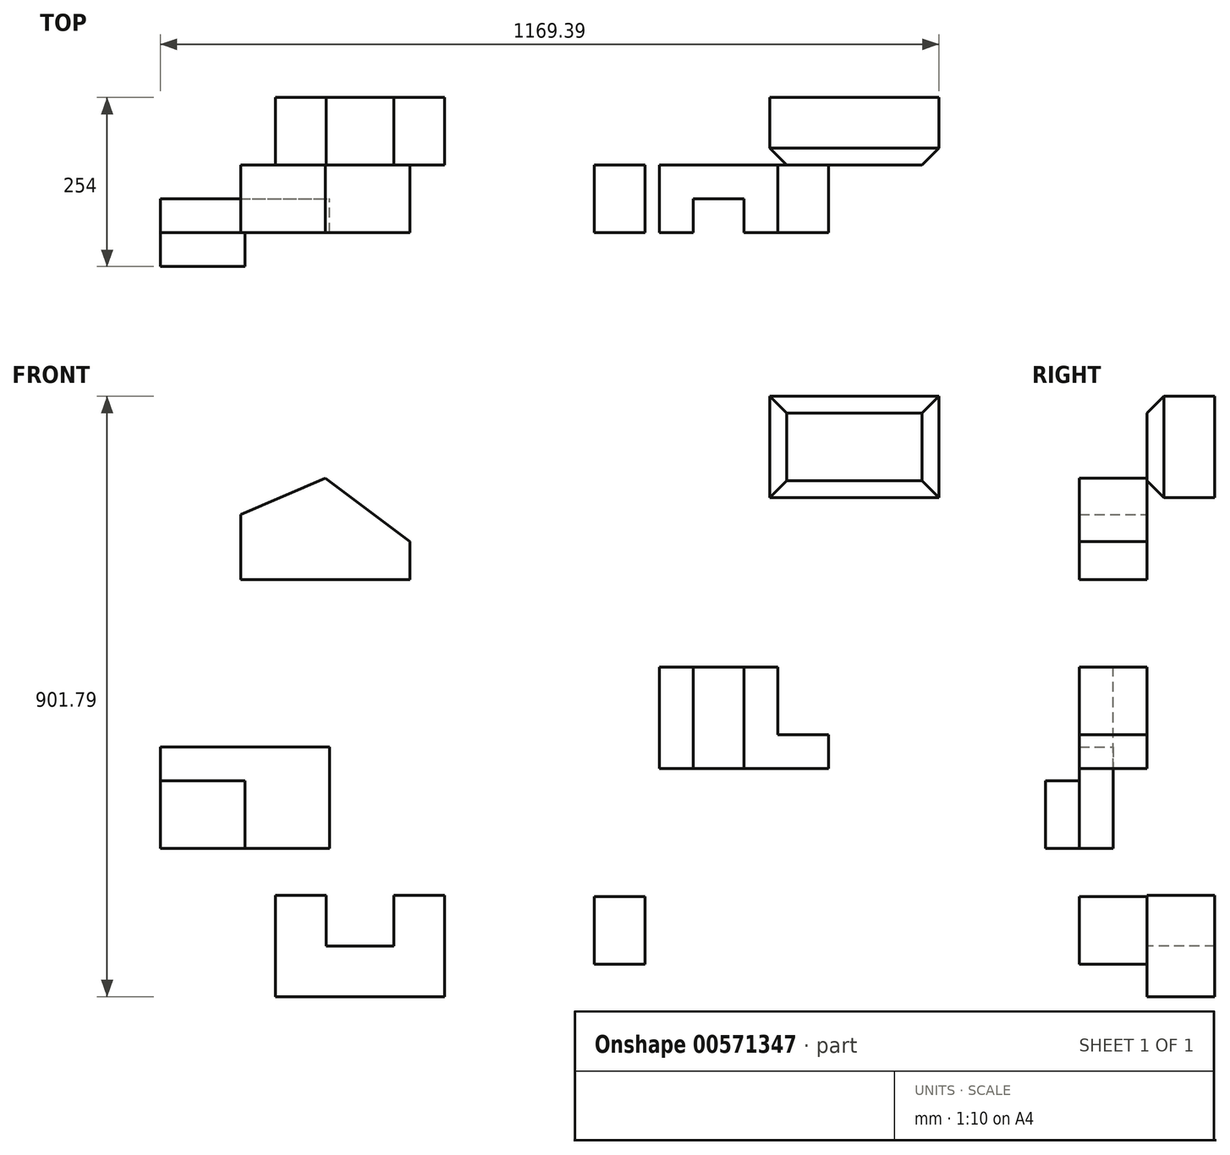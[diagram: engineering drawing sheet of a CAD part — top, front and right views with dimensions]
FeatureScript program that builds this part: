
annotation { "Feature Type Name" : "Feature", "Feature Type Description" : "" }
export const myFeature = defineFeature(function(context is Context, id is Id, definition is map)
    precondition{}
    {
        {
            var Q0;
            Q0=qCreatedBy(makeId("Front.planeOp"),FACE);
            var sketch = newSketch(context, id + "F0", { "sketchPlane" : qUnion([Q0])});
            skLineSegment(sketch, "E0", {"start": v(0, 0) * mm, "end": v(254, 0) * mm});
            skLineSegment(sketch, "E1", {"start": v(254, 152.4) * mm, "end": v(254, 0) * mm});
            skLineSegment(sketch, "E2", {"start": v(254, 152.4) * mm, "end": v(177.8, 152.4) * mm});
            skLineSegment(sketch, "E3", {"start": v(177.8, 152.4) * mm, "end": v(177.8, 76.2) * mm});
            skLineSegment(sketch, "E4", {"start": v(177.8, 76.2) * mm, "end": v(76.2, 76.2) * mm});
            skLineSegment(sketch, "E5", {"start": v(76.2, 76.2) * mm, "end": v(76.2, 152.4) * mm});
            skLineSegment(sketch, "E6", {"start": v(76.2, 132.49) * mm, "end": v(76.2, 125.11) * mm});
            skLineSegment(sketch, "E7", {"start": v(76.2, 152.4) * mm, "end": v(0, 152.4) * mm});
            skLineSegment(sketch, "E8", {"start": v(0, 0) * mm, "end": v(0, 152.4) * mm});
            skSolve(sketch);
        }
        {
            var Q0;
            Q0=makeQuery(id+"F0.imprint","IMPRINT",FACE,{"disambiguationData":[TD([[makeQuery(id+"F0.imprint","IMPRINT",EDGE,{"derivedFrom":sQuery(id+"F0.wireOp",EDGE,"E0")}),1.0]])]});
            extrude(context, id + "F1", {"entities" : qUnion([Q0]), "oppositeDirection" : true, "depth" : 101.6 * mm, "offsetDistance" : 25.4 * mm});
        }
        {
            var Q0;
            Q0=qCreatedBy(makeId("Front.planeOp"),FACE);
            var sketch = newSketch(context, id + "F2", { "sketchPlane" : qUnion([Q0])});
            skLineSegment(sketch, "E9.bottom", {"start": v(-172.87, 375.03) * mm, "end": v(81.13, 375.03) * mm});
            skLineSegment(sketch, "E9.top", {"start": v(-172.87, 222.63) * mm, "end": v(81.13, 222.63) * mm});
            skLineSegment(sketch, "E9.left", {"start": v(-172.87, 375.03) * mm, "end": v(-172.87, 222.63) * mm});
            skLineSegment(sketch, "E9.right", {"start": v(81.13, 375.03) * mm, "end": v(81.13, 222.63) * mm});
            skSolve(sketch);
        }
        {
            var Q0;
            Q0=makeQuery(id+"F2.imprint","IMPRINT",FACE,{"disambiguationData":[TD([[makeQuery(id+"F2.imprint","IMPRINT",EDGE,{"derivedFrom":sQuery(id+"F2.wireOp",EDGE,"E9.bottom")}),-1.0]])]});
            extrude(context, id + "F3", {"entities" : qUnion([Q0]), "depth" : 152.4 * mm, "offsetDistance" : 25.4 * mm});
        }
        {
            var Q0;
            Q0=makeQuery(id+"F3.opExtrude","SWEPT_FACE",FACE,{"disambiguationData":[OSD([sQuery(id+"F2.wireOp",EDGE,"E9.bottom")])]});
            var sketch = newSketch(context, id + "F4", { "sketchPlane" : qUnion([Q0])});
            skLineSegment(sketch, "E10.bottom", {"start": v(81.13, -152.4) * mm, "end": v(-45.87, -152.4) * mm});
            skLineSegment(sketch, "E10.top", {"start": v(81.13, -101.6) * mm, "end": v(-45.87, -101.6) * mm});
            skLineSegment(sketch, "E10.left", {"start": v(81.13, -152.4) * mm, "end": v(81.13, -101.6) * mm});
            skLineSegment(sketch, "E10.right", {"start": v(-45.87, -152.4) * mm, "end": v(-45.87, -101.6) * mm});
            skLineSegment(sketch, "E11.bottom", {"start": v(81.13, 0) * mm, "end": v(-172.87, 0) * mm});
            skLineSegment(sketch, "E11.top", {"start": v(81.13, -39.4) * mm, "end": v(-172.87, -39.4) * mm});
            skLineSegment(sketch, "E11.left", {"start": v(81.13, 0) * mm, "end": v(81.13, -39.4) * mm});
            skLineSegment(sketch, "E11.right", {"start": v(-172.87, 0) * mm, "end": v(-172.87, -39.4) * mm});
            skSolve(sketch);
        }
        {
            var Q0;
            Q0=makeQuery(id+"F4.imprint","IMPRINT",FACE,{"disambiguationData":[TD([[makeQuery(id+"F4.imprint","IMPRINT",EDGE,{"derivedFrom":sQuery(id+"F4.wireOp",EDGE,"E10.bottom")}),1.0]])]});
            extrude(context, id + "F5", {"entities" : qUnion([Q0]), "operationType" : NewBodyOperationType.REMOVE, "oppositeDirection" : true, "depth" : 152.4 * mm, "offsetDistance" : 25.4 * mm});
        }
        {
            var Q0;
            Q0=makeQuery(id+"F3.opExtrude","CAP_FACE",FACE,{"disambiguationData":[OSD([sQuery(id+"F2.wireOp",EDGE,"E9.bottom"),sQuery(id+"F2.wireOp",EDGE,"E9.top"),sQuery(id+"F2.wireOp",EDGE,"E9.left"),sQuery(id+"F2.wireOp",EDGE,"E9.right")])],"isStart":false});
            var sketch = newSketch(context, id + "F6", { "sketchPlane" : qUnion([Q0])});
            skLineSegment(sketch, "E12.bottom", {"start": v(-172.87, 375.03) * mm, "end": v(-45.87, 375.03) * mm});
            skLineSegment(sketch, "E12.top", {"start": v(-172.87, 324.4) * mm, "end": v(-45.87, 324.4) * mm});
            skLineSegment(sketch, "E12.left", {"start": v(-172.87, 375.03) * mm, "end": v(-172.87, 324.4) * mm});
            skLineSegment(sketch, "E12.right", {"start": v(-45.87, 375.03) * mm, "end": v(-45.87, 324.4) * mm});
            skSolve(sketch);
        }
        {
            var Q0;
            Q0 = qSketchRegion(id + "F6", true);
            extrude(context, id + "F7", {"entities" : qUnion([Q0]), "operationType" : NewBodyOperationType.REMOVE, "oppositeDirection" : true, "depth" : 50.8 * mm, "offsetDistance" : 25.4 * mm});
        }
        {
            var Q0;
            Q0 = qSketchRegion(id + "F2", true);
            extrude(context, id + "F8", {"entities" : qUnion([Q0]), "operationType" : NewBodyOperationType.REMOVE, "depth" : 50.8 * mm, "offsetDistance" : 25.4 * mm});
        }
        {
            var Q0;
            Q0=qCreatedBy(makeId("Front.planeOp"),FACE);
            var sketch = newSketch(context, id + "F9", { "sketchPlane" : qUnion([Q0])});
            skLineSegment(sketch, "E13.bottom", {"start": v(576.31, 342.9) * mm, "end": v(830.31, 342.9) * mm});
            skLineSegment(sketch, "E13.top", {"start": v(576.31, 495.3) * mm, "end": v(830.31, 495.3) * mm});
            skLineSegment(sketch, "E13.left", {"start": v(576.31, 342.9) * mm, "end": v(576.31, 495.3) * mm});
            skLineSegment(sketch, "E13.right", {"start": v(830.31, 342.9) * mm, "end": v(830.31, 495.3) * mm});
            skLineSegment(sketch, "E14.right", {"start": v(830.31, 508.38) * mm, "end": v(830.31, 393.7) * mm});
            skLineSegment(sketch, "E15.bottom", {"start": v(754.11, 495.3) * mm, "end": v(830.31, 495.3) * mm});
            skLineSegment(sketch, "E15.top", {"start": v(754.11, 393.7) * mm, "end": v(830.31, 393.7) * mm});
            skLineSegment(sketch, "E15.left", {"start": v(754.11, 495.3) * mm, "end": v(754.11, 393.7) * mm});
            skLineSegment(sketch, "E15.right", {"start": v(830.31, 495.3) * mm, "end": v(830.31, 393.7) * mm});
            skSolve(sketch);
        }
        {
            var Q0;
            Q0=makeQuery(id+"F9.imprint","IMPRINT",FACE,{"disambiguationData":[TD([[makeQuery(id+"F9.imprint","IMPRINT",EDGE,{"derivedFrom":sQuery(id+"F9.wireOp",EDGE,"E13.bottom")}),1.0]])]});
            extrude(context, id + "F10", {"entities" : qUnion([Q0]), "depth" : 101.6 * mm, "offsetDistance" : 25.4 * mm});
        }
        {
            var Q0;
            Q0=makeQuery(id+"F10.opExtrude","SWEPT_FACE",FACE,{"disambiguationData":[OSD([sQuery(id+"F9.wireOp",EDGE,"E13.top")])]});
            var sketch = newSketch(context, id + "F11", { "sketchPlane" : qUnion([Q0])});
            skLineSegment(sketch, "E16.bottom", {"start": v(627.11, -101.6) * mm, "end": v(703.31, -101.6) * mm});
            skLineSegment(sketch, "E16.top", {"start": v(627.11, -50.8) * mm, "end": v(703.31, -50.8) * mm});
            skLineSegment(sketch, "E16.left", {"start": v(627.11, -101.6) * mm, "end": v(627.11, -50.8) * mm});
            skLineSegment(sketch, "E16.right", {"start": v(703.31, -101.6) * mm, "end": v(703.31, -50.8) * mm});
            skSolve(sketch);
        }
        {
            var Q0;
            Q0=makeQuery(id+"F11.imprint","IMPRINT",FACE,{"disambiguationData":[TD([[makeQuery(id+"F11.imprint","IMPRINT",EDGE,{"derivedFrom":sQuery(id+"F11.wireOp",EDGE,"E16.bottom")}),1.0]])]});
            extrude(context, id + "F12", {"entities" : qUnion([Q0]), "operationType" : NewBodyOperationType.REMOVE, "oppositeDirection" : true, "depth" : 152.4 * mm, "offsetDistance" : 25.4 * mm});
        }
        {
            var Q0;
            Q0=qCreatedBy(makeId("Front.planeOp"),FACE);
            var sketch = newSketch(context, id + "F13", { "sketchPlane" : qUnion([Q0])});
            skLineSegment(sketch, "E17.bottom", {"start": v(478.85, 48.86) * mm, "end": v(732.85, 48.86) * mm});
            skLineSegment(sketch, "E17.top", {"start": v(478.85, 201.26) * mm, "end": v(732.85, 201.26) * mm});
            skLineSegment(sketch, "E17.left", {"start": v(478.85, 48.86) * mm, "end": v(478.85, 201.26) * mm});
            skLineSegment(sketch, "E17.right", {"start": v(732.85, 48.86) * mm, "end": v(732.85, 201.26) * mm});
            skLineSegment(sketch, "E18.bottom", {"start": v(478.85, 150.46) * mm, "end": v(555.05, 150.46) * mm});
            skLineSegment(sketch, "E18.top", {"start": v(478.85, 48.86) * mm, "end": v(555.05, 48.86) * mm});
            skLineSegment(sketch, "E18.left", {"start": v(478.85, 150.46) * mm, "end": v(478.85, 48.86) * mm});
            skLineSegment(sketch, "E18.right", {"start": v(555.05, 150.46) * mm, "end": v(555.05, 48.86) * mm});
            skLineSegment(sketch, "E19.bottom", {"start": v(732.85, 201.26) * mm, "end": v(656.65, 201.26) * mm});
            skLineSegment(sketch, "E19.top", {"start": v(732.85, 99.66) * mm, "end": v(656.65, 99.66) * mm});
            skLineSegment(sketch, "E19.left", {"start": v(732.85, 201.26) * mm, "end": v(732.85, 99.66) * mm});
            skLineSegment(sketch, "E19.right", {"start": v(656.65, 201.26) * mm, "end": v(656.65, 99.66) * mm});
            skSolve(sketch);
        }
        {
            var Q0;
            Q0=makeQuery(id+"F13.imprint","IMPRINT",FACE,{"disambiguationData":[TD([[makeQuery(id+"F13.imprint","IMPRINT",EDGE,{"derivedFrom":sQuery(id+"F13.wireOp",EDGE,"E17.bottom")}),1.0]])]});
            extrude(context, id + "F14", {"entities" : qUnion([Q0]), "depth" : 101.6 * mm, "offsetDistance" : 25.4 * mm});
        }
        {
            var Q0;
            Q0=qCreatedBy(makeId("Front.planeOp"),FACE);
            var sketch = newSketch(context, id + "F15", { "sketchPlane" : qUnion([Q0])});
            skLineSegment(sketch, "E20.bottom", {"start": v(-52.27, 778.82) * mm, "end": v(201.73, 778.82) * mm});
            skLineSegment(sketch, "E20.top", {"start": v(-52.27, 626.42) * mm, "end": v(201.73, 626.42) * mm});
            skLineSegment(sketch, "E20.left", {"start": v(-52.27, 778.82) * mm, "end": v(-52.27, 626.42) * mm});
            skLineSegment(sketch, "E20.right", {"start": v(201.73, 778.82) * mm, "end": v(201.73, 626.42) * mm});
            skLineSegment(sketch, "E21", {"start": v(74.73, 778.82) * mm, "end": v(201.73, 683.83) * mm});
            skLineSegment(sketch, "E22", {"start": v(74.73, 778.82) * mm, "end": v(-52.27, 724.15) * mm});
            skSolve(sketch);
        }
        {
            var Q0;
            {var subQ1=sQuery(id+"F15.wireOp",EDGE,"E20.top");Q0=makeQuery(id+"F15.imprint","IMPRINT",FACE,{"disambiguationData":[TD([[makeQuery(id+"F15.imprint","IMPRINT",EDGE,{"derivedFrom":subQ1}),1.0]])]});}
            extrude(context, id + "F16", {"entities" : qUnion([Q0]), "depth" : 101.6 * mm, "offsetDistance" : 25.4 * mm});
        }
        {
            var Q0;
            Q0=qCreatedBy(makeId("Front.planeOp"),FACE);
            var sketch = newSketch(context, id + "F17", { "sketchPlane" : qUnion([Q0])});
            skLineSegment(sketch, "E23.bottom", {"start": v(742.52, 901.79) * mm, "end": v(996.52, 901.79) * mm});
            skLineSegment(sketch, "E23.top", {"start": v(742.52, 749.39) * mm, "end": v(996.52, 749.39) * mm});
            skLineSegment(sketch, "E23.left", {"start": v(742.52, 901.79) * mm, "end": v(742.52, 749.39) * mm});
            skLineSegment(sketch, "E23.right", {"start": v(996.52, 901.79) * mm, "end": v(996.52, 749.39) * mm});
            skSolve(sketch);
        }
        {
            var Q0;
            Q0=makeQuery(id+"F17.imprint","IMPRINT",FACE,{"disambiguationData":[TD([[makeQuery(id+"F17.imprint","IMPRINT",EDGE,{"derivedFrom":sQuery(id+"F17.wireOp",EDGE,"E23.bottom")}),-1.0]])]});
            extrude(context, id + "F18", {"entities" : qUnion([Q0]), "oppositeDirection" : true, "depth" : 101.6 * mm, "offsetDistance" : 25.4 * mm});
        }
        {
            var Q0;
            Q0=makeQuery(id+"F18.opExtrude","CAP_FACE",FACE,{"disambiguationData":[OSD([sQuery(id+"F17.wireOp",EDGE,"E23.bottom"),sQuery(id+"F17.wireOp",EDGE,"E23.top"),sQuery(id+"F17.wireOp",EDGE,"E23.left"),sQuery(id+"F17.wireOp",EDGE,"E23.right")])],"isStart":true});
            chamfer(context, id + "F19", {"entities" : qUnion([Q0]), "width" : 25.4 * mm, "tangentPropagation" : true});
        }
    });
